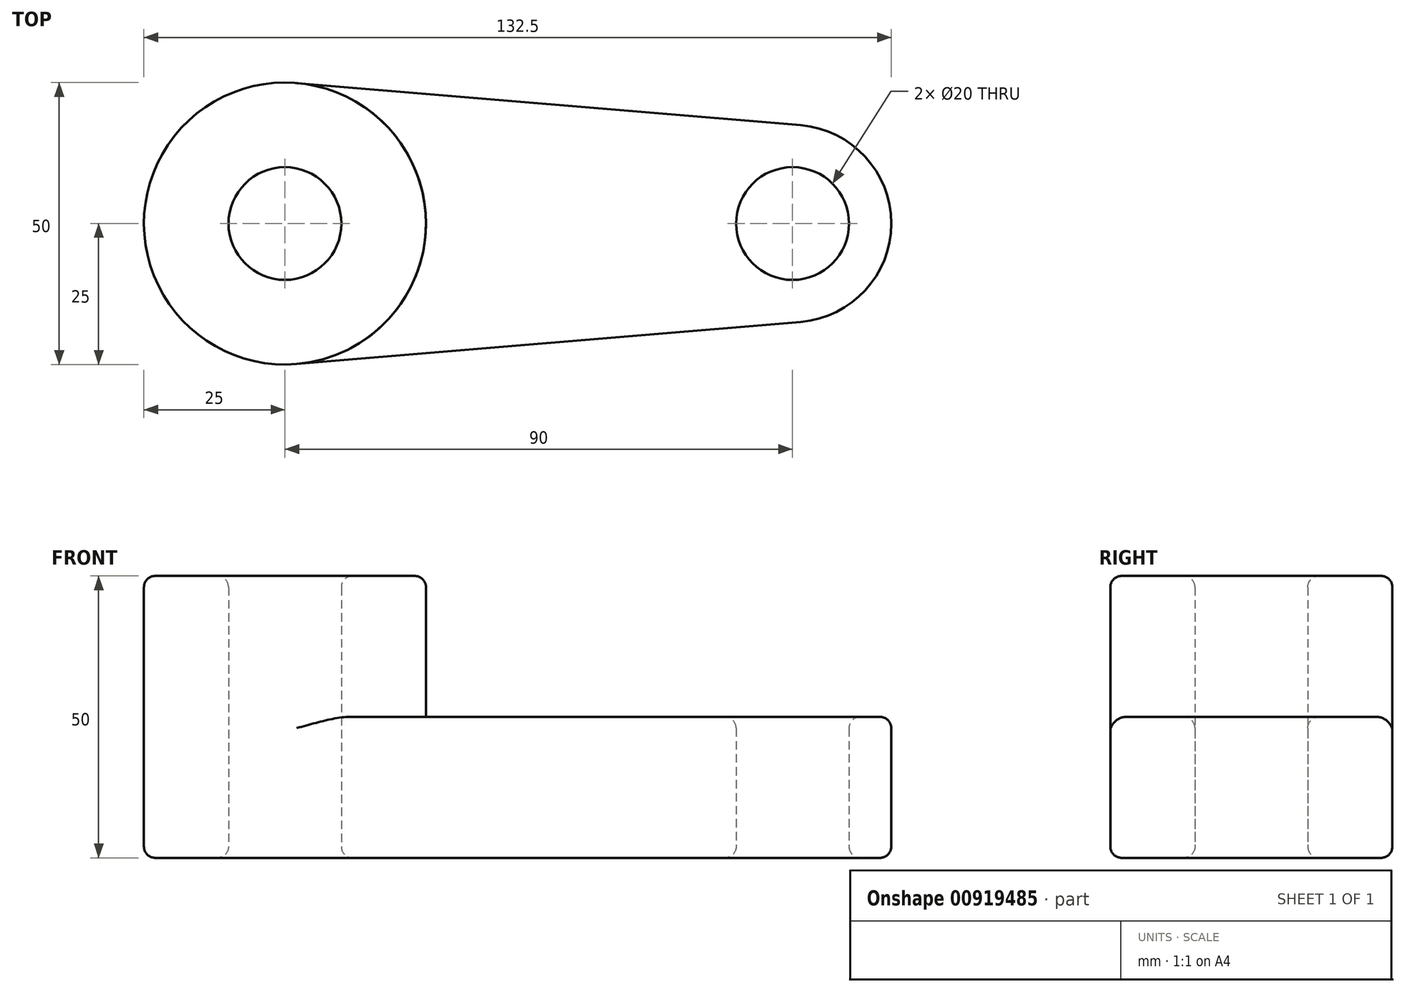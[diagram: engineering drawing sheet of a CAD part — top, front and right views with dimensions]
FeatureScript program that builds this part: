
annotation { "Feature Type Name" : "Feature", "Feature Type Description" : "" }
export const myFeature = defineFeature(function(context is Context, id is Id, definition is map)
    precondition{}
    {
        {
            var Q0;
            Q0=qCreatedBy(makeId("Top.planeOp"),FACE);
            var sketch = newSketch(context, id + "F0", { "sketchPlane" : qUnion([Q0])});
            skCircle(sketch, "E0", {"center": v(0, 0) * mm, "radius": 25 * mm});
            skCircle(sketch, "E1", {"center": v(90, 0) * mm, "radius": 17.5 * mm});
            skLineSegment(sketch, "E2", {"start": v(2.08, 24.91) * mm, "end": v(91.46, 17.44) * mm});
            skLineSegment(sketch, "E3", {"start": v(2.08, -24.91) * mm, "end": v(91.46, -17.44) * mm});
            skCircle(sketch, "E4", {"center": v(0, 0) * mm, "radius": 10 * mm});
            skCircle(sketch, "E5", {"center": v(90, 0) * mm, "radius": 10 * mm});
            skSolve(sketch);
        }
        {
            var Q0;
            {var subQ0=sQuery(id+"F0.wireOp",EDGE,"E2");Q0=makeQuery(id+"F0.imprint","IMPRINT",FACE,{"disambiguationData":[TD([[makeQuery(id+"F0.imprint","IMPRINT",EDGE,{"derivedFrom":subQ0}),-1.0]])]});}
            var Q1;
            Q1=makeQuery(id+"F0.imprint","IMPRINT",FACE,{"disambiguationData":[TD([[makeQuery(id+"F0.imprint","IMPRINT",EDGE,{"derivedFrom":sQuery(id+"F0.wireOp",EDGE,"E5")}),-1.0]])]});
            var Q2;
            Q2=makeQuery(id+"F0.imprint","IMPRINT",FACE,{"disambiguationData":[TD([[makeQuery(id+"F0.imprint","IMPRINT",EDGE,{"derivedFrom":sQuery(id+"F0.wireOp",EDGE,"E4")}),-1.0]])]});
            extrude(context, id + "F1", {"entities" : qUnion([Q0, Q1, Q2]), "depth" : 25 * mm, "offsetDistance" : 25 * mm});
        }
        {
            var Q0;
            Q0 = qSketchRegion(id + "F0", true);
            var sketch = newSketch(context, id + "F2", { "sketchPlane" : qUnion([Q0])});
            skSolve(sketch);
        }
        {
            var Q0;
            Q0=makeQuery(id+"F2.imprint","IMPRINT",FACE,{"disambiguationData":[TD([[makeQuery(id+"F2.imprint","IMPRINT",EDGE,{"derivedFrom":makeQuery(id+"F0.imprint","IMPRINT",EDGE,{"derivedFrom":sQuery(id+"F0.wireOp",EDGE,"E4")})}),-1.0]])]});
            extrude(context, id + "F3", {"entities" : qUnion([Q0]), "operationType" : NewBodyOperationType.ADD, "depth" : 50 * mm, "offsetDistance" : 25 * mm});
        }
        {
            var Q0;
            Q0=makeQuery(id+"F3.opExtrude","CAP_EDGE",EDGE,{"disambiguationData":[OSD([sQuery(id+"F0.wireOp",EDGE,"E4")])],"isStart":false});
            var Q1;
            Q1=makeQuery(id+"F3.opExtrude","CAP_EDGE",EDGE,{"disambiguationData":[OSD([sQuery(id+"F0.wireOp",EDGE,"E0")])],"isStart":false});
            var Q2;
            Q2=makeQuery(id+"F1.opExtrude","CAP_EDGE",EDGE,{"disambiguationData":[OSD([sQuery(id+"F0.wireOp",EDGE,"E5")])],"isStart":false});
            fillet(context, id + "F4", {"entities" : qUnion([Q0, Q1, Q2]), "radius" : 2 * mm, "tangentPropagation" : true, "allowEdgeOverflow" : false});
        }
        {
            var Q0;
            Q0=makeQuery(id+"F1.opExtrude","CAP_EDGE",EDGE,{"disambiguationData":[OSD([sQuery(id+"F0.wireOp",EDGE,"E2")])],"isStart":false});
            var Q1;
            Q1=makeQuery(id+"F1.opExtrude","CAP_EDGE",EDGE,{"disambiguationData":[OSD([sQuery(id+"F0.wireOp",EDGE,"E3")])],"isStart":false});
            var Q2;
            Q2=makeQuery(id+"F1.opExtrude","CAP_EDGE",EDGE,{"disambiguationData":[OSD([sQuery(id+"F0.wireOp",EDGE,"E1")])],"isStart":false});
            fillet(context, id + "F5", {"entities" : qUnion([Q0, Q1, Q2]), "radius" : 2 * mm, "tangentPropagation" : true, "allowEdgeOverflow" : false});
        }
        {
            var Q0;
            Q0=makeQuery(id+"F1.opExtrude","CAP_EDGE",EDGE,{"disambiguationData":[OSD([sQuery(id+"F0.wireOp",EDGE,"E3")])],"isStart":true});
            var Q1;
            Q1=makeQuery(id+"F1.opExtrude","CAP_EDGE",EDGE,{"disambiguationData":[OSD([sQuery(id+"F0.wireOp",EDGE,"E5")])],"isStart":true});
            var Q2;
            Q2=makeQuery(id+"F1.opExtrude","CAP_EDGE",EDGE,{"disambiguationData":[OSD([sQuery(id+"F0.wireOp",EDGE,"E4")])],"isStart":true});
            fillet(context, id + "F6", {"entities" : qUnion([Q0, Q1, Q2]), "radius" : 2 * mm, "tangentPropagation" : true, "allowEdgeOverflow" : false});
        }
    });
